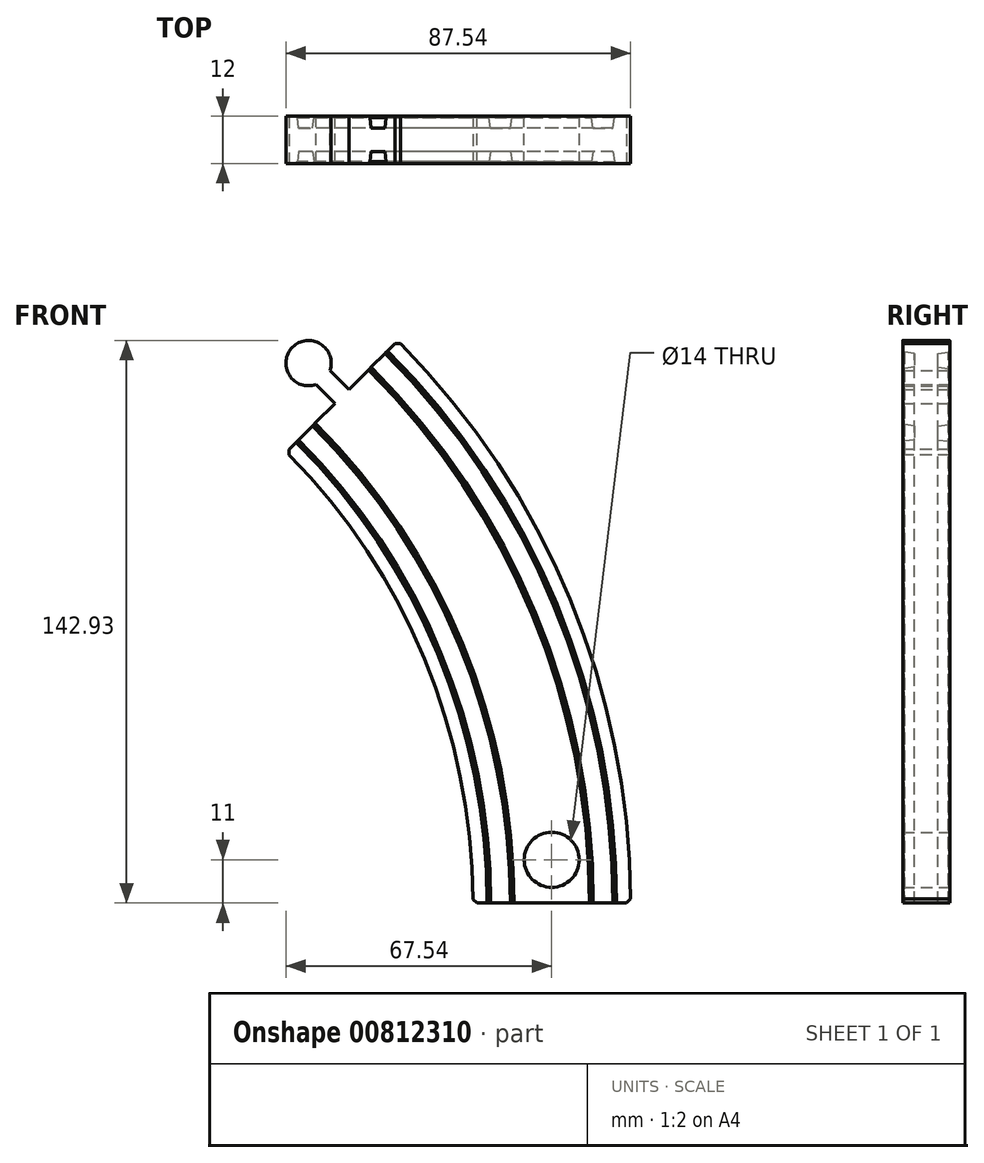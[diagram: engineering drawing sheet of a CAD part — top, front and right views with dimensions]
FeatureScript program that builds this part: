
annotation { "Feature Type Name" : "Feature", "Feature Type Description" : "" }
export const myFeature = defineFeature(function(context is Context, id is Id, definition is map)
    precondition{}
    {
        {
            var Q0;
            Q0=qCreatedBy(makeId("Top.planeOp"),FACE);
            var sketch = newSketch(context, id + "F0", { "sketchPlane" : qUnion([Q0])});
            skLineSegment(sketch, "E0.bottom", {"start": v(-20, 6) * mm, "end": v(20, 6) * mm});
            skLineSegment(sketch, "E0.top", {"start": v(-20, -6) * mm, "end": v(20, -6) * mm});
            skLineSegment(sketch, "E0.left", {"start": v(-20, 6) * mm, "end": v(-20, -6) * mm});
            skLineSegment(sketch, "E0.right", {"start": v(20, 6) * mm, "end": v(20, -6) * mm});
            skLineSegment(sketch, "E1", {"start": v(10.53, 3) * mm, "end": v(15.53, 3) * mm});
            skLineSegment(sketch, "E2", {"start": v(-15.53, 3) * mm, "end": v(-10.53, 3) * mm});
            skLineSegment(sketch, "E3", {"start": v(-20, 6) * mm, "end": v(20, -6) * mm, "construction": true});
            skLineSegment(sketch, "E4", {"start": v(-10.53, 3) * mm, "end": v(-10, 6) * mm});
            skLineSegment(sketch, "E5", {"start": v(-15.53, 3) * mm, "end": v(-16, 6) * mm});
            skLineSegment(sketch, "E6", {"start": v(10.53, 3) * mm, "end": v(10, 6) * mm});
            skLineSegment(sketch, "E7", {"start": v(15.53, 3) * mm, "end": v(16, 6) * mm});
            skLineSegment(sketch, "E8", {"start": v(15.53, -3) * mm, "end": v(10.53, -3) * mm});
            skLineSegment(sketch, "E9", {"start": v(15.53, -3) * mm, "end": v(16, -6) * mm});
            skLineSegment(sketch, "E10", {"start": v(10.53, -3) * mm, "end": v(10, -6) * mm});
            skLineSegment(sketch, "E11", {"start": v(-10.53, -3) * mm, "end": v(-15.53, -3) * mm});
            skLineSegment(sketch, "E12", {"start": v(-10.53, -3) * mm, "end": v(-10, -6) * mm});
            skLineSegment(sketch, "E13", {"start": v(-15.53, -3) * mm, "end": v(-16, -6) * mm});
            skLineSegment(sketch, "E14", {"start": v(10, 6) * mm, "end": v(10, -6) * mm, "construction": true});
            skLineSegment(sketch, "E15", {"start": v(16, 6) * mm, "end": v(16, -6) * mm, "construction": true});
            skLineSegment(sketch, "E16", {"start": v(10.53, 3) * mm, "end": v(10.53, -6) * mm, "construction": true});
            skLineSegment(sketch, "E17", {"start": v(-15.53, 3) * mm, "end": v(-15.53, -6) * mm, "construction": true});
            skSolve(sketch);
        }
        {
            var Q0;
            Q0=qCreatedBy(makeId("Front.planeOp"),FACE);
            var sketch = newSketch(context, id + "F1", { "sketchPlane" : qUnion([Q0])});
            skArc(sketch, "E18", {"start": v(0, 0) * mm, "mid": v(-13.85, 69.65) * mm, "end": v(-53.3, 128.7) * mm});
            skLineSegment(sketch, "E19", {"start": v(-182, 0) * mm, "end": v(-6.72, 175.28) * mm, "construction": true});
            skSolve(sketch);
        }
        {
            var Q0;
            Q0=makeQuery(id+"F0.imprint","IMPRINT",FACE,{"disambiguationData":[TD([[makeQuery(id+"F0.imprint","IMPRINT",EDGE,{"derivedFrom":sQuery(id+"F0.wireOp",EDGE,"E0.top")}),1.0]])]});
            var Q1;
            Q1=sQuery(id+"F1.wireOp",EDGE,"E18");
            sweep(context, id + "F2", {"profiles" : qUnion([Q0]), "path" : qUnion([Q1])});
        }
        {
            var Q0;
            Q0=makeQuery(id+"F2.opSweep","SWEPT_EDGE",EDGE,{"disambiguationData":[OSD([sQuery(id+"F0.wireOp",EDGE,"E0.bottom"),sQuery(id+"F0.wireOp",EDGE,"E4"),sQuery(id+"F1.wireOp",EDGE,"QheDVgyy-v1Xf-DTUT-CkoZ-R19I37jAeaWV")])]});
            var Q1;
            Q1=makeQuery(id+"F2.opSweep","SWEPT_EDGE",EDGE,{"disambiguationData":[OSD([sQuery(id+"F0.wireOp",EDGE,"E0.bottom"),sQuery(id+"F0.wireOp",EDGE,"E5"),sQuery(id+"F1.wireOp",EDGE,"QheDVgyy-v1Xf-DTUT-CkoZ-R19I37jAeaWV")])]});
            var Q2;
            Q2=makeQuery(id+"F2.opSweep","SWEPT_EDGE",EDGE,{"disambiguationData":[OSD([sQuery(id+"F0.wireOp",EDGE,"E0.bottom"),sQuery(id+"F0.wireOp",EDGE,"E6"),sQuery(id+"F1.wireOp",EDGE,"QheDVgyy-v1Xf-DTUT-CkoZ-R19I37jAeaWV")])]});
            var Q3;
            Q3=makeQuery(id+"F2.opSweep","SWEPT_EDGE",EDGE,{"disambiguationData":[OSD([sQuery(id+"F0.wireOp",EDGE,"E0.bottom"),sQuery(id+"F0.wireOp",EDGE,"E7"),sQuery(id+"F1.wireOp",EDGE,"QheDVgyy-v1Xf-DTUT-CkoZ-R19I37jAeaWV")])]});
            var Q4;
            Q4=makeQuery(id+"F2.opSweep","SWEPT_EDGE",EDGE,{"disambiguationData":[OSD([sQuery(id+"F0.wireOp",EDGE,"E0.top"),sQuery(id+"F0.wireOp",EDGE,"E10"),sQuery(id+"F1.wireOp",EDGE,"E18")])]});
            var Q5;
            Q5=makeQuery(id+"F2.opSweep","SWEPT_EDGE",EDGE,{"disambiguationData":[OSD([sQuery(id+"F0.wireOp",EDGE,"E0.top"),sQuery(id+"F0.wireOp",EDGE,"E9"),sQuery(id+"F1.wireOp",EDGE,"E18")])]});
            var Q6;
            Q6=makeQuery(id+"F2.opSweep","SWEPT_EDGE",EDGE,{"disambiguationData":[OSD([sQuery(id+"F0.wireOp",EDGE,"E0.top"),sQuery(id+"F0.wireOp",EDGE,"E13"),sQuery(id+"F1.wireOp",EDGE,"E18")])]});
            var Q7;
            Q7=makeQuery(id+"F2.opSweep","SWEPT_EDGE",EDGE,{"disambiguationData":[OSD([sQuery(id+"F0.wireOp",EDGE,"E0.top"),sQuery(id+"F0.wireOp",EDGE,"E12"),sQuery(id+"F1.wireOp",EDGE,"E18")])]});
            chamfer(context, id + "F3", {"entities" : qUnion([Q0, Q1, Q2, Q3, Q4, Q5, Q6, Q7]), "width" : 0.5 * mm, "tangentPropagation" : true});
        }
        {
            var Q0;
            Q0=qCreatedBy(makeId("Front.planeOp"),FACE);
            var sketch = newSketch(context, id + "F4", { "sketchPlane" : qUnion([Q0])});
            skLineSegment(sketch, "E20.0", {"start": v(-46.59, 135.41) * mm, "end": v(-60.02, 121.98) * mm});
            skSolve(sketch);
        }
        {
            var Q0;
            Q0=qCreatedBy(makeId("Front.planeOp"),FACE);
            var sketch = newSketch(context, id + "F5", { "sketchPlane" : qUnion([Q0])});
            skLineSegment(sketch, "E21.0", {"start": v(9.5, 0) * mm, "end": v(-9.5, 0) * mm});
            skLineSegment(sketch, "E22.bottom", {"start": v(3.5, 0) * mm, "end": v(-3.5, 0) * mm});
            skLineSegment(sketch, "E22.top", {"start": v(3.5, 5) * mm, "end": v(-3.5, 5) * mm});
            skLineSegment(sketch, "E22.left", {"start": v(3.5, 0) * mm, "end": v(3.5, 5) * mm});
            skLineSegment(sketch, "E22.right", {"start": v(-3.5, 0) * mm, "end": v(-3.5, 5) * mm});
            skLineSegment(sketch, "E23", {"start": v(9.5, 0) * mm, "end": v(3.5, 0) * mm, "construction": true});
            skLineSegment(sketch, "E24", {"start": v(-3.5, 0) * mm, "end": v(-9.5, 0) * mm, "construction": true});
            skCircle(sketch, "E25", {"center": v(0, 11) * mm, "radius": 7 * mm});
            skPoint(sketch, "E25.centerSnap0", {"position": v(0, 5) * mm});
            skSolve(sketch);
        }
        {
            var Q0;
            {var subQ0=sQuery(id+"F1.wireOp",EDGE,"QheDVgyy-v1Xf-DTUT-CkoZ-R19I37jAeaWV");var subQ1=sQuery(id+"F0.wireOp",EDGE,"E0.bottom");Q0=makeQuery(id+"F2.opSweep","SWEPT_FACE",FACE,{"disambiguationData":[OSD([subQ1,subQ0]),TDD([makeQuery(id+"F0.imprint","IMPRINT",EDGE,{"disambiguationData":[TD([[makeQuery(id+"F0.imprint","INTERSECT",VERTEX,{"derivedFrom":[subQ1,sQuery(id+"F0.wireOp",EDGE,"E4")]}),-1.0]])],"derivedFrom":subQ1}),subQ0])]});}
            var sketch = newSketch(context, id + "F6", { "sketchPlane" : qUnion([Q0])});
            skCircle(sketch, "E26.0", {"center": v(0, 11) * mm, "radius": 7 * mm});
            skLineSegment(sketch, "E27.0", {"start": v(3.5, 0) * mm, "end": v(3.5, 5) * mm});
            skLineSegment(sketch, "E28.0", {"start": v(-3.5, 0) * mm, "end": v(-3.5, 5) * mm});
            skLineSegment(sketch, "E29.0", {"start": v(-3.5, 5) * mm, "end": v(3.5, 5) * mm});
            skLineSegment(sketch, "E30.0", {"start": v(-9.5, 0) * mm, "end": v(9.5, 0) * mm});
            skSolve(sketch);
        }
        {
            var Q0;
            {var subQ5=sQuery(id+"F6.wireOp",EDGE,"E29.0");Q0=makeQuery(id+"F6.imprint","IMPRINT",FACE,{"disambiguationData":[TD([[makeQuery(id+"F6.imprint","IMPRINT",EDGE,{"derivedFrom":subQ5}),1.0]])]});}
            var Q1;
            {var subQ0=sQuery(id+"F6.wireOp",EDGE,"E27.0");var subQ1=sQuery(id+"F6.wireOp",EDGE,"E26.0");var subQ2=makeQuery(id+"F6.imprint","INTERSECT",VERTEX,{"derivedFrom":[subQ1,subQ0]});Q1=makeQuery(id+"F6.imprint","IMPRINT",FACE,{"disambiguationData":[TD([[makeQuery(id+"F6.imprint","IMPRINT",EDGE,{"disambiguationData":[TD([[subQ2,-1.0]])],"derivedFrom":subQ1}),1.0]])]});}
            var Q2;
            {var subQ5=sQuery(id+"F6.wireOp",EDGE,"E29.0");Q2=makeQuery(id+"F6.imprint","IMPRINT",FACE,{"disambiguationData":[TD([[makeQuery(id+"F6.imprint","IMPRINT",EDGE,{"derivedFrom":subQ5}),-1.0]])]});}
            extrude(context, id + "F7", {"entities" : qUnion([Q0, Q1, Q2]), "operationType" : NewBodyOperationType.REMOVE, "oppositeDirection" : true, "depth" : 25.4 * mm, "offsetDistance" : 25.4 * mm});
        }
        {
            var Q0;
            Q0=makeQuery(id+"F2.opSweep","CAP_EDGE",EDGE,{"disambiguationData":[OSD([sQuery(id+"F0.wireOp",EDGE,"E0.right"),sQuery(id+"F1.wireOp",VERTEX,"QheDVgyy-v1Xf-DTUT-CkoZ-R19I37jAeaWV.start")])],"isStart":false});
            var Q1;
            Q1=makeQuery(id+"F2.opSweep","CAP_EDGE",EDGE,{"disambiguationData":[OSD([sQuery(id+"F0.wireOp",EDGE,"E0.left"),sQuery(id+"F1.wireOp",VERTEX,"QheDVgyy-v1Xf-DTUT-CkoZ-R19I37jAeaWV.start")])],"isStart":false});
            var Q2;
            Q2=makeQuery(id+"F2.opSweep","CAP_EDGE",EDGE,{"disambiguationData":[OSD([sQuery(id+"F0.wireOp",EDGE,"E0.left"),sQuery(id+"F1.wireOp",VERTEX,"QheDVgyy-v1Xf-DTUT-CkoZ-R19I37jAeaWV.end")])],"isStart":true});
            var Q3;
            Q3=makeQuery(id+"F2.opSweep","CAP_EDGE",EDGE,{"disambiguationData":[OSD([sQuery(id+"F0.wireOp",EDGE,"E0.right"),sQuery(id+"F1.wireOp",VERTEX,"QheDVgyy-v1Xf-DTUT-CkoZ-R19I37jAeaWV.end")])],"isStart":true});
            chamfer(context, id + "F8", {"entities" : qUnion([Q0, Q1, Q2, Q3]), "width" : 1 * mm, "tangentPropagation" : true});
        }
        {
            var Q0;
            {var subQ0=sQuery(id+"F1.wireOp",EDGE,"E18");var subQ1=sQuery(id+"F0.wireOp",EDGE,"E0.bottom");Q0=makeQuery(id+"F2.opSweep","SWEPT_FACE",FACE,{"disambiguationData":[OSD([subQ1,subQ0]),TDD([makeQuery(id+"F0.imprint","IMPRINT",EDGE,{"disambiguationData":[TD([[makeQuery(id+"F0.imprint","INTERSECT",VERTEX,{"derivedFrom":[subQ1,sQuery(id+"F0.wireOp",EDGE,"E4")]}),-1.0]])],"derivedFrom":subQ1}),subQ0])]});}
            var sketch = newSketch(context, id + "F9", { "sketchPlane" : qUnion([Q0])});
            skLineSegment(sketch, "E31", {"start": v(51.54, 130.46) * mm, "end": v(56.49, 135.41) * mm});
            skLineSegment(sketch, "E32", {"start": v(56.49, 135.41) * mm, "end": v(60.02, 131.88) * mm});
            skLineSegment(sketch, "E33", {"start": v(60.02, 131.88) * mm, "end": v(55.07, 126.93) * mm});
            skLineSegment(sketch, "E34", {"start": v(51.54, 130.46) * mm, "end": v(46.59, 135.41) * mm, "construction": true});
            skLineSegment(sketch, "E35", {"start": v(55.07, 126.93) * mm, "end": v(60.02, 121.98) * mm, "construction": true});
            skLineSegment(sketch, "E36", {"start": v(53.3, 128.7) * mm, "end": v(61.8, 137.18) * mm, "construction": true});
            skCircle(sketch, "E37", {"center": v(61.8, 137.18) * mm, "radius": 5.75 * mm});
            skSolve(sketch);
        }
        {
            var Q0;
            {var subQ0=sQuery(id+"F4.wireOp",EDGE,"y3DwgqY9-x9Yp-s0zT-CjDQ-IHoX7M89SHfb");var subQ1=sQuery(id+"F4.wireOp",EDGE,"XYbCKtlu-qh1t-nVi3-P5wv-khNMWSoX9qSB");var subQ2=makeQuery(id+"F4.imprint","INTERSECT",VERTEX,{"derivedFrom":[subQ1,subQ0]});Q0=makeQuery(id+"F4.imprint","IMPRINT",FACE,{"disambiguationData":[TD([[makeQuery(id+"F4.imprint","IMPRINT",EDGE,{"disambiguationData":[TD([[subQ2,1.0]])],"derivedFrom":subQ1}),-1.0]])]});}
            var Q1;
            {var subQ0=sQuery(id+"F4.wireOp",EDGE,"rqF1hGhq-thtG-Dqzb-XRaq-cd5KwwhKuCuG");var subQ1=sQuery(id+"F4.wireOp",EDGE,"E20.0");var subQ2=makeQuery(id+"F4.imprint","INTERSECT",VERTEX,{"derivedFrom":[subQ1,subQ0]});Q1=makeQuery(id+"F4.imprint","IMPRINT",FACE,{"disambiguationData":[TD([[makeQuery(id+"F4.imprint","IMPRINT",EDGE,{"disambiguationData":[TD([[subQ2,-1.0]])],"derivedFrom":subQ1}),-1.0]])]});}
            var Q2;
            {var subQ0=sQuery(id+"F4.wireOp",EDGE,"y3DwgqY9-x9Yp-s0zT-CjDQ-IHoX7M89SHfb");var subQ1=sQuery(id+"F4.wireOp",EDGE,"E20.0");var subQ2=makeQuery(id+"F4.imprint","INTERSECT",VERTEX,{"derivedFrom":[subQ1,subQ0]});Q2=makeQuery(id+"F4.imprint","IMPRINT",FACE,{"disambiguationData":[TD([[makeQuery(id+"F4.imprint","IMPRINT",EDGE,{"disambiguationData":[TD([[subQ2,1.0]])],"derivedFrom":subQ1}),-1.0]])]});}
            var Q3;
            {var subQ0=sQuery(id+"F4.wireOp",EDGE,"y3DwgqY9-x9Yp-s0zT-CjDQ-IHoX7M89SHfb");var subQ1=sQuery(id+"F4.wireOp",EDGE,"XYbCKtlu-qh1t-nVi3-P5wv-khNMWSoX9qSB");var subQ2=makeQuery(id+"F4.imprint","INTERSECT",VERTEX,{"derivedFrom":[subQ1,subQ0]});Q3=makeQuery(id+"F4.imprint","IMPRINT",FACE,{"disambiguationData":[TD([[makeQuery(id+"F4.imprint","IMPRINT",EDGE,{"disambiguationData":[TD([[subQ2,1.0]])],"derivedFrom":subQ1}),1.0]])]});}
            var Q4;
            {var subQ0=sQuery(id+"F4.wireOp",EDGE,"XYbCKtlu-qh1t-nVi3-P5wv-khNMWSoX9qSB");var subQ1=sQuery(id+"F4.wireOp",EDGE,"rqF1hGhq-thtG-Dqzb-XRaq-cd5KwwhKuCuG");var subQ2=makeQuery(id+"F4.imprint","INTERSECT",VERTEX,{"derivedFrom":[subQ1,subQ0]});Q4=makeQuery(id+"F4.imprint","IMPRINT",FACE,{"disambiguationData":[TD([[makeQuery(id+"F4.imprint","IMPRINT",EDGE,{"disambiguationData":[TD([[subQ2,1.0]])],"derivedFrom":subQ1}),-1.0]])]});}
            var Q5;
            {var subQ0=sQuery(id+"F4.wireOp",EDGE,"XYbCKtlu-qh1t-nVi3-P5wv-khNMWSoX9qSB");var subQ1=sQuery(id+"F4.wireOp",EDGE,"rqF1hGhq-thtG-Dqzb-XRaq-cd5KwwhKuCuG");var subQ2=makeQuery(id+"F4.imprint","INTERSECT",VERTEX,{"derivedFrom":[subQ1,subQ0]});Q5=makeQuery(id+"F4.imprint","IMPRINT",FACE,{"disambiguationData":[TD([[makeQuery(id+"F4.imprint","IMPRINT",EDGE,{"disambiguationData":[TD([[subQ2,1.0]])],"derivedFrom":subQ1}),1.0]])]});}
            var Q6;
            {var subQ0=sQuery(id+"F9.wireOp",EDGE,"E31");Q6=makeQuery(id+"F9.imprint","IMPRINT",FACE,{"disambiguationData":[TD([[makeQuery(id+"F9.imprint","IMPRINT",EDGE,{"derivedFrom":subQ0}),-1.0]])]});}
            var Q7;
            {var subQ0=sQuery(id+"F9.wireOp",EDGE,"E37");var subQ1=sQuery(id+"F9.wireOp",EDGE,"E32");var subQ2=makeQuery(id+"F9.imprint","INTERSECT",VERTEX,{"disambiguationData":[OD(0.0)],"derivedFrom":[subQ1,subQ0]});Q7=makeQuery(id+"F9.imprint","IMPRINT",FACE,{"disambiguationData":[TD([[makeQuery(id+"F9.imprint","IMPRINT",EDGE,{"disambiguationData":[TD([[subQ2,-1.0]])],"derivedFrom":subQ1}),1.0]])]});}
            var Q8;
            {var subQ0=sQuery(id+"F9.wireOp",EDGE,"E37");var subQ1=sQuery(id+"F9.wireOp",EDGE,"E32");var subQ2=makeQuery(id+"F9.imprint","INTERSECT",VERTEX,{"disambiguationData":[OD(0.0)],"derivedFrom":[subQ1,subQ0]});Q8=makeQuery(id+"F9.imprint","IMPRINT",FACE,{"disambiguationData":[TD([[makeQuery(id+"F9.imprint","IMPRINT",EDGE,{"disambiguationData":[TD([[subQ2,-1.0]])],"derivedFrom":subQ1}),-1.0]])]});}
            extrude(context, id + "F10", {"entities" : qUnion([Q0, Q1, Q2, Q3, Q4, Q5, Q6, Q7, Q8]), "operationType" : NewBodyOperationType.ADD, "oppositeDirection" : true, "depth" : 12 * mm, "offsetDistance" : 25.4 * mm});
        }
    });
